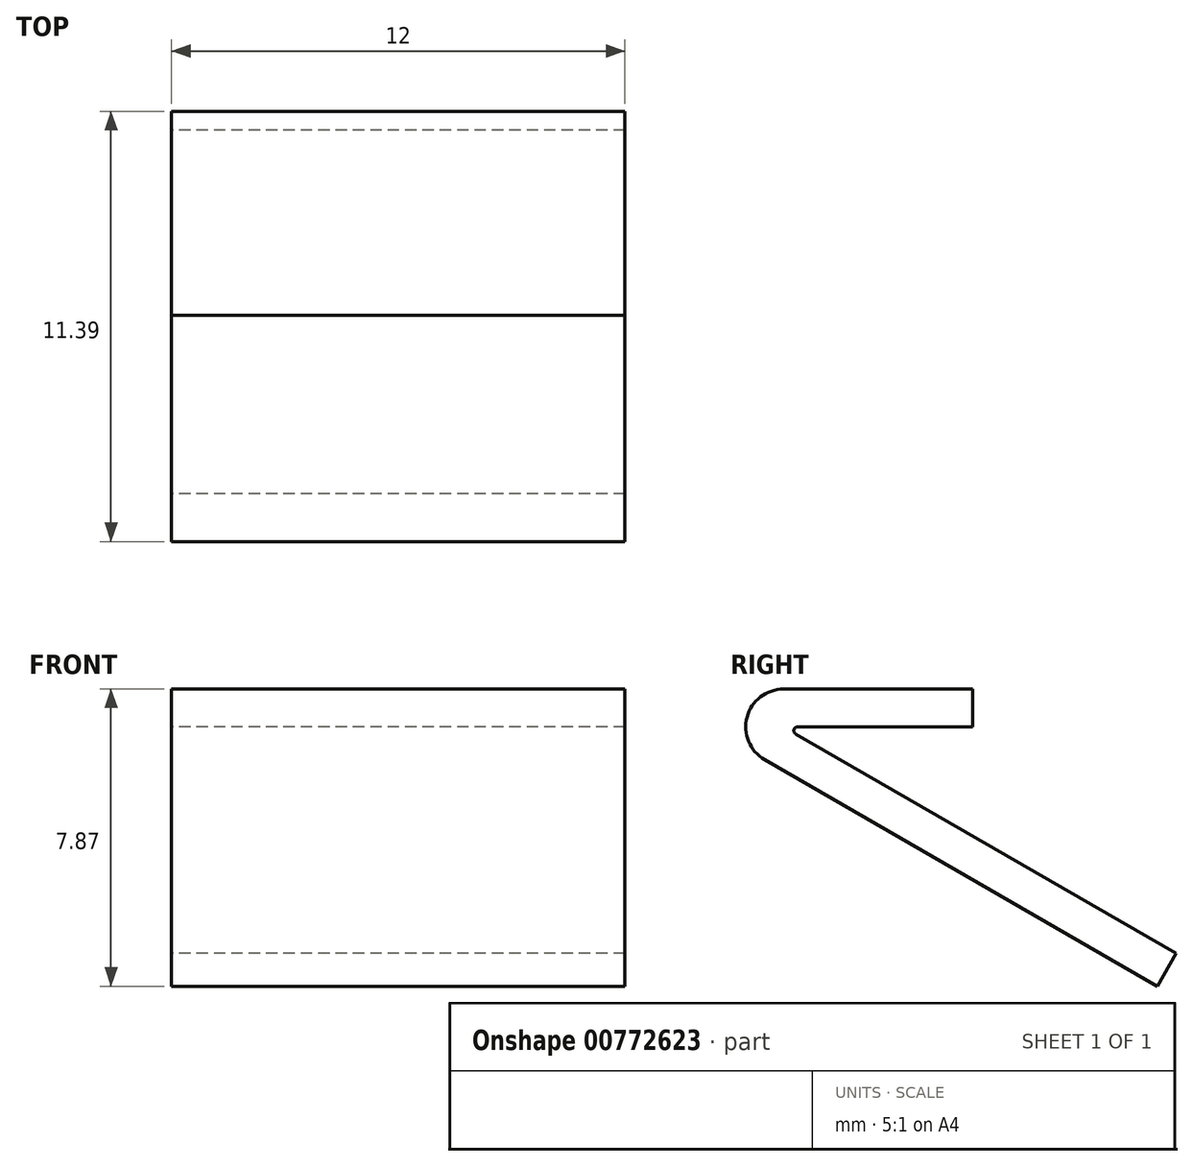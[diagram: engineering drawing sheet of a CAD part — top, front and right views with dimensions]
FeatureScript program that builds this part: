
annotation { "Feature Type Name" : "Feature", "Feature Type Description" : "" }
export const myFeature = defineFeature(function(context is Context, id is Id, definition is map)
    precondition{}
    {
        {
            var Q0;
            Q0=qCreatedBy(makeId("Right.planeOp"),FACE);
            var sketch = newSketch(context, id + "F0", { "sketchPlane" : qUnion([Q0])});
            skLineSegment(sketch, "E0", {"start": v(0, 0) * mm, "end": v(0.5, 0.87) * mm});
            skLineSegment(sketch, "E1", {"start": v(0.5, 0.87) * mm, "end": v(-9.57, 6.68) * mm});
            skLineSegment(sketch, "E2", {"start": v(-9.52, 6.87) * mm, "end": v(-4.9, 6.87) * mm});
            skLineSegment(sketch, "E3", {"start": v(-4.9, 6.87) * mm, "end": v(-4.9, 7.87) * mm});
            skLineSegment(sketch, "E4", {"start": v(-4.9, 7.87) * mm, "end": v(-9.9, 7.87) * mm});
            skLineSegment(sketch, "E5", {"start": v(-10.4, 6) * mm, "end": v(0, 0) * mm});
            skPoint(sketch, "E6.visualSharp", {"position": v(-13.62, 7.87) * mm});
            skArc(sketch, "E6.filletArc", {"start": v(-9.9, 7.87) * mm, "mid": v(-10.86, 7.12) * mm, "end": v(-10.4, 6) * mm});
            skArc(sketch, "E7.filletArc", {"start": v(-9.52, 6.87) * mm, "mid": v(-9.62, 6.8) * mm, "end": v(-9.57, 6.68) * mm});
            skSolve(sketch);
        }
        {
            var Q0;
            Q0=makeQuery(id+"F0.imprint","IMPRINT",FACE,{"disambiguationData":[TD([[makeQuery(id+"F0.imprint","IMPRINT",EDGE,{"derivedFrom":sQuery(id+"F0.wireOp",EDGE,"E0")}),1.0]])]});
            extrude(context, id + "F1", {"entities" : qUnion([Q0]), "endBound" : BoundingType.SYMMETRIC, "depth" : 12 * mm, "offsetDistance" : 25 * mm});
        }
    });
